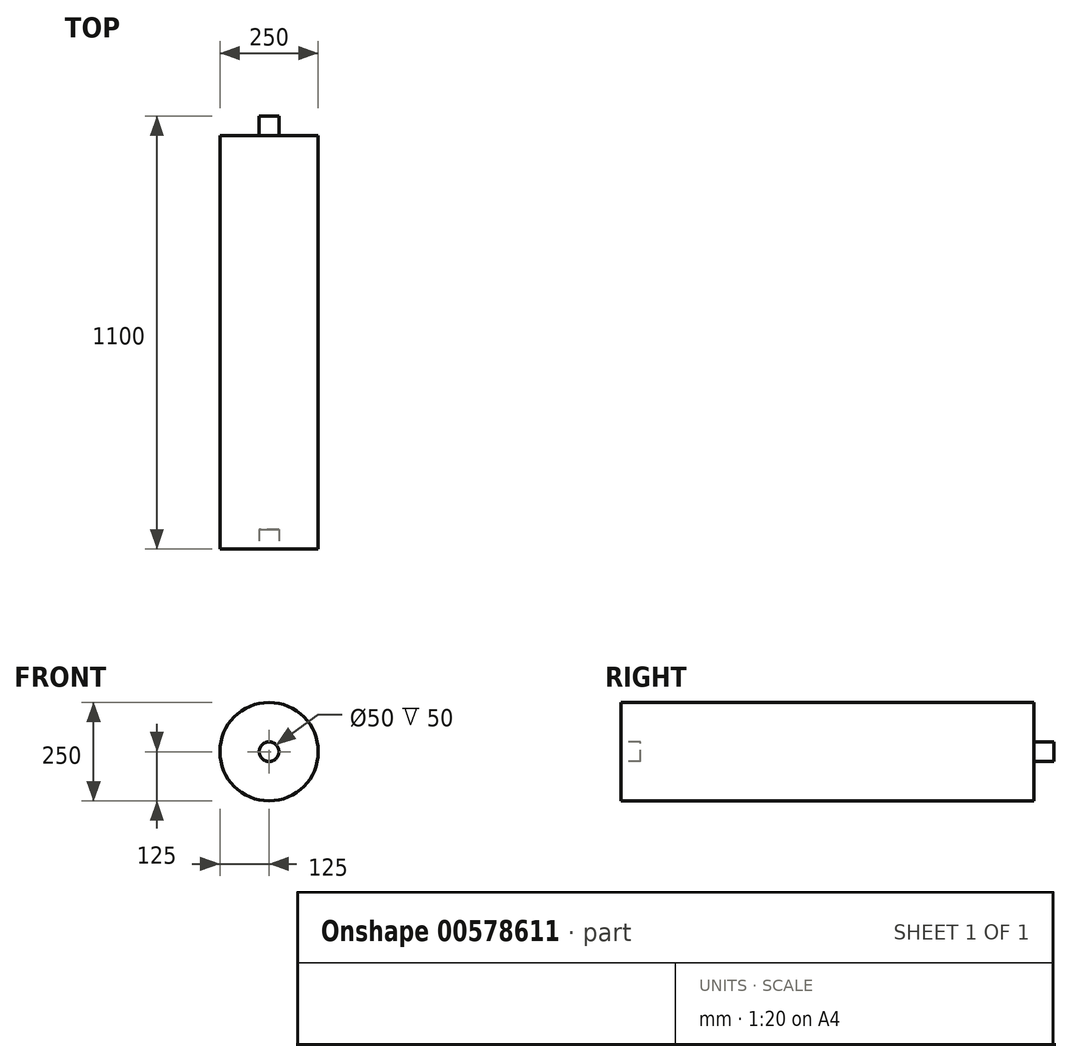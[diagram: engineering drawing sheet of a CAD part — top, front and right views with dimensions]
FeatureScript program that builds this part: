
annotation { "Feature Type Name" : "Feature", "Feature Type Description" : "" }
export const myFeature = defineFeature(function(context is Context, id is Id, definition is map)
    precondition{}
    {
        {
            var Q0;
            Q0=qCreatedBy(makeId("Front.planeOp"),FACE);
            var sketch = newSketch(context, id + "F0", { "sketchPlane" : qUnion([Q0])});
            skCircle(sketch, "E0", {"center": v(0, 0) * mm, "radius": 125 * mm});
            skSolve(sketch);
        }
        {
            var Q0;
            Q0=qSketchRegion(id+"F0",true);
            extrude(context, id + "F1", {"entities" : qUnion([Q0]), "oppositeDirection" : true, "depth" : 1100 * mm});
        }
        {
            var Q0;
            Q0=makeQuery(id+"F1.opExtrude","CAP_FACE",FACE,{"disambiguationData":[OSD([sQuery(id+"F0.wireOp",EDGE,"E0")])],"isStart":true});
            var sketch = newSketch(context, id + "F2", { "sketchPlane" : qUnion([Q0])});
            skCircle(sketch, "E1", {"center": v(0, 0) * mm, "radius": 25 * mm});
            skSolve(sketch);
        }
        {
            var Q0;
            Q0=qSketchRegion(id+"F2",true);
            extrude(context, id + "F3", {"entities" : qUnion([Q0]), "operationType" : NewBodyOperationType.REMOVE, "oppositeDirection" : true, "depth" : 50 * mm});
        }
        {
            var Q0;
            Q0=makeQuery(id+"F1.opExtrude","CAP_FACE",FACE,{"disambiguationData":[OSD([sQuery(id+"F0.wireOp",EDGE,"E0")])],"isStart":false});
            var sketch = newSketch(context, id + "F4", { "sketchPlane" : qUnion([Q0])});
            skCircle(sketch, "E2.0", {"center": v(0, 0) * mm, "radius": 25 * mm});
            skSolve(sketch);
        }
        {
            var Q0;
            Q0=makeQuery(id+"F4.imprint","IMPRINT",FACE,{"disambiguationData":[TD([[makeQuery(id+"F4.imprint","IMPRINT",EDGE,{"derivedFrom":sQuery(id+"F4.wireOp",EDGE,"E2.0")}),-1.0]])]});
            extrude(context, id + "F5", {"entities" : qUnion([Q0]), "operationType" : NewBodyOperationType.REMOVE, "oppositeDirection" : true, "depth" : 50 * mm});
        }
    });
